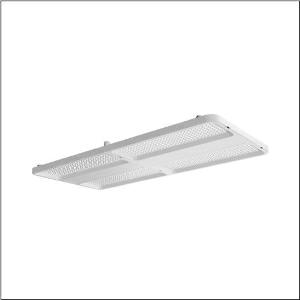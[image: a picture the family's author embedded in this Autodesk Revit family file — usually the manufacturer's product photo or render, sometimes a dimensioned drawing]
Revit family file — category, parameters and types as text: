
# Revit family: highbay_21_maxi_52hn11db6lda
name_source: partatom
category: Lighting Fixtures
units: mm (PartAtom-declared; Revit-internal decimal feet)

## family parameters
Cut with Voids When Loaded = No
Host = Face
Light Source = No
Part Type = Normal
Room Calculation Point = No
Round Connector Dimension = Use Diameter
Shared = No

## types (1)
- --- (1 x LED, 4100 lm, 22.6 W, 6500K)
    Apparent Load = 23 VA
    CIE Flux Codes = 89 97 99 100 100
    Color Rendering = 80
    Color Temperature = 6500K
    Default Elevation = 1800 mm
    Description = high bay luminaire Highbay 21 maxi; direct symmetric narrow distribution, light control with lens of PMMA; UGR ≤ 19 (X = 4H | Y = 8H | S = 0.25H | reflection values 70/50/20); luminous flux: 27.140lm; light colour: 865, colour temperature: 6500K, MacAdam ≤ 3 SDCM (initial), colour rendering: CRI > 80; luminous efficacy: 188,5lm/W; rated service life: 75.000h (L80) at AT= ta max; control: DALI 2; luminaire connection: terminal, 5-pole, max. 2.5mm² (cable entry for one cable, Ø 8.5..16mm); mains connection: 230..240V, AC/DC 0/50..60Hz; connected load: 144W; protection rating (complete): IP66; insulation class (complete): insulation class I (protective earthing); protection symbol: D; impact resistance: IK08; certification: CE, ENEC, VDE, UKCA; luminaire for central battery installations according to EN 60598-2-22, internal wiring halogen-free; luminaire LABS conformity tested according to VDMA 24364:2018-05; Suitable for use in the food industry according to the specifications of IFS-Food, HACCP and/or BRC; housing frame of high-performance plastic PA6, matt traffic white (RAL 9016); cover of PMMA; dimension (LxWxH): 946 x 442 x 72mm; permissible operating ambient temperature: -40..+65°C (reducing of maximum allowable ambient temperature of 5°C with ceiling mounting); packaging unit: 1 piece; (delivery without accessories; please order mounting accessories separately)
    Height = 72 mm  [stored 0.23622 ft]
    Lamp = 1 x LED
    Lamp Light Flux = 4100 lm
    Lamp Power = 22.6 W
    Lamp count = 1
    Length = 946 mm
    Luminous efficacy = 181 lm/W
    Manufacturer = Siteco
    ModVariant = No
    Model = 52HN11DB6LDA
    Mounting Place = Ceiling
    Mounting Type = Pendant
    Number of Poles = 1
    OnlyDefault = Yes
    Power Factor = 1
    Product Name = Highbay 21 maxi
    Product group = high bay luminaire
    ProductGroupID = 902
    Protection Class = Protection class I
    Protection Degree = IP 66
    RLX_Detail_Level = 1
    RLX_Emergency_Light_Flux = 0 lm
    RLX_Emergency_Type = 0
    RLX_Emergency_Type_DB = No
    RlxData = <blob elided: 127973 chars, md5=42458d8c>
    Socket = socket
    Standby Power = 0 W
    System Light Flux = 4100 lm
    System Power = 23 W
    Type Comments = : DC mode (central or group accumulator) initial emergency light level
    Type Image = l_1363244.jpg
    URL = http://relux.com
    VarID = @adj_003297
    Voltage = 0 V
    Weight = 0.00 kg
    Width = 442 mm

note: [stored X ft] marks values corroborated as IEEE doubles in the binary element streams (Revit-internal decimal feet)

## geometry (parser evidence)
native form markers: Blend x4, Sweep x10
no freeform markers — native parametric forms only
